# Revit family: CL 55 Pusher feed-head 2 speeds (a)
name_source: partatom
category: Equipement spécialisé
revit_build: Autodesk Revit LT 2015 (Build: 20140606_1530(x64)
units: mm (PartAtom-declared; Revit-internal decimal feet)

## types (3) — shared parameters
Apparent Power = 0 VA
Description = COUPE-LEGUMES
Fabricant = ROBOT COUPE
Height = 1135 mm
Phase = 3
Speeds (Rpm) = 375 & 750
UP Delpth = 645 mm
UP Height = 1320 mm
URL = www.robot-coupe.com
Watts = 1100 W
Weight = 43.6 Kg
water = Connector
zero-valued in all types: Cold water supply, Cold water supply height, Top, Used water, Waste water height

## per-type parameters (varying)
| type | Amps | Cycle | Depth | Electrique connexion | Modèle | Volts | Width |
| CL55 Pusher feed-head 2 speeds  400/50/3 | 2.7 A | 50 Hz | 366 mm | 154 mm  [stored 0.505249 ft] | CL55 Pusher feed-head 2 speeds | 400 V | 720 mm |
| CL55 Pusher feed-head 2 speeds  220/60/3 | 5.3 A | 60 Hz | 720 mm | 153 mm | CL55 Pusher feed-head 2 speeds | 220 V | 365 mm |
| CL55 Pusher feed-head 2 speeds  380/60/3 | 2.7 A | 60 Hz | 720 mm | 153 mm | CL55 Pusher-feed head 2 speeds | 380 V | 365 mm |

note: [stored X ft] marks values corroborated as IEEE doubles in the binary element streams (Revit-internal decimal feet)

## geometry (parser evidence)
native form markers: Blend x77, Sweep x5
no freeform markers — native parametric forms only
